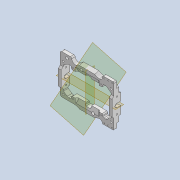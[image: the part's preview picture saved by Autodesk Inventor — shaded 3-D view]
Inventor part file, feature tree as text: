
AUTODESK INVENTOR PART (.ipt)
format: ipt  version: 2020 (Build 240168000, 168)  size: 982,528 bytes
history: native  units: mm
features: sketch x22, extrude x20, projected_geometry x20, reference x17, fillet x14, other x12, mirror x8, thicken_offset x8, plane x3, chamfer x3, hole x2
ambient origin geometry x8: Origin, YZ Plane, XZ Plane, XY Plane, X Axis, Y Axis, Z Axis, Center Point
bodies: Solid1 (feature_tree)
feature tree (129):
  extrude  "Extrusion1"  Depth=30.0mm
  extrude  "Extrusion2"  Depth=56.0mm
  plane  "Work Plane1"
  mirror  "Mirror1"
  extrude  "Extrusion3"  Depth=20.0mm
  extrude  "Extrusion4"  Depth=4.0mm TaperAngle=0.0deg
  plane  "Work Plane2"
  extrude  "Extrusion5"  Depth=10.0mm
  extrude  "Extrusion6"  Depth=1.5mm
  plane  "Work Plane3"
  mirror  "Mirror2"
  extrude  "Extrusion7"  Depth=80.0mm TaperAngle=0.0deg
  mirror  "Mirror3"
  fillet  "Fillet1"  Radius=3.0mm
  thicken_offset  "Thicken1"
  thicken_offset  "Thicken2"
  extrude  "Extrusion8"  Depth=6.0mm TaperAngle=0.0deg
  mirror  "Mirror4"
  extrude  "Extrusion10"  Depth=10.0mm
  thicken_offset  "Thicken3"
  mirror  "Mirror5"
  thicken_offset  "Thicken4"
  extrude  "Extrusion11"  Depth=3.5mm
  extrude  "Extrusion12"  Depth=10.0mm TaperAngle=0.0deg
  fillet  "Fillet4"  Radius=8.0mm
  extrude  "Extrusion13"  Depth=1.0mm
  extrude  "Extrusion14"  Depth=1.0mm
  extrude  "Extrusion15"  Depth=4.0mm
  extrude  "Extrusion16"  Depth=1.0mm
  thicken_offset  "Thicken5"
  fillet  "Fillet7"  Radius=1.5mm
  fillet  "Fillet8"  Radius=4.0mm
  fillet  "Fillet9"  Radius=3.0mm
  fillet  "Fillet10"  Radius=10.0mm
  fillet  "Fillet11"  Radius=4.0mm
  fillet  "Fillet12"  Radius=1.0mm
  extrude  "Extrusion17"  Depth=0.5mm
  mirror  "Mirror6"
  extrude  "Extrusion18"  Depth=10.0mm
  hole  "Hole1"  [1 undecoded]
  extrude  "Extrusion19"  Depth=2.8mm
  thicken_offset  "Thicken6"
  hole  "Hole2"  [1 undecoded]
  extrude  "Extrusion20"  Depth=6.0mm TaperAngle=0.0deg
  extrude  "Extrusion21"  Depth=1.0mm
  mirror  "Mirror7"
  fillet  "Fillet13"  Radius=6.0mm
  mirror  "Mirror8"
  fillet  "Fillet14"  Radius=15.0mm
  fillet  "Fillet15"  Radius=2.8mm
  chamfer  "Chamfer1"  Distance=6.0mm
  fillet  "Fillet16"  Radius=1.5mm
  chamfer  "Chamfer2"  Distance=1.5mm
  chamfer  "Chamfer3"  Distance=4.0mm
  fillet  "Fillet17"  Radius=3.0mm
  fillet  "Fillet18"  Radius=4.0mm
  thicken_offset  "Thicken7"
  thicken_offset  "Thicken8"
  sketch  "Sketch1"  dims[d0=50.0mm d1=30.0mm]
  reference  "Reference1"
  reference  "Reference2"
  sketch  "Sketch2"  dims[d2=36.0mm d3=56.0mm]
  projected_geometry  "Projected Loop1"
  reference  "Reference3"
  sketch  "Sketch3"  dims[d4=4.0mm d5=0.0mm d6=20.0mm]
  reference  "Reference4"
  sketch  "Sketch4"  dims[d7=8.0mm d8=4.0mm d9=0.0mm]
  reference  "Reference5"
  reference  "Reference6"
  sketch  "Sketch5"  dims[d10=10.0mm d11=4.0mm]
  projected_geometry  "Projected Loop2"
  projected_geometry  "Projected Loop3"
  projected_geometry  "Projected Loop4"
  reference  "Reference7"
  sketch  "Sketch6"  dims[d12=80.0mm d13=0.0mm d14=1.5mm]
  projected_geometry  "Projected Loop5"
  projected_geometry  "Projected Loop6"
  sketch  "Sketch7"  dims[d15=1.5mm d16=80.0mm d17=0.0mm d18=3.0mm]
  projected_geometry  "Projected Loop7"
  projected_geometry  "Projected Loop8"
  sketch  "Sketch8"  dims[d19=3.0mm d20=6.0mm d21=0.0mm]
  projected_geometry  "Projected Loop9"
  reference  "Reference8"
  reference  "Reference9"
  sketch  "Sketch10"  dims[d22=10.0mm d23=0.0mm d24=3.5mm]
  projected_geometry  "Projected Loop11"
  sketch  "Sketch11"  dims[d25=5.0mm d26=3.5mm]
  projected_geometry  "Projected Loop13"
  projected_geometry  "Projected Loop14"
  sketch  "Sketch12"  dims[d27=5.0mm d28=10.0mm d29=0.0mm d30=8.0mm]
  reference  "Reference11"
  sketch  "Sketch13"  dims[d32=1.0mm d33=1.0mm]
  projected_geometry  "Projected Loop15"
  sketch  "Sketch14"  dims[d34=1.0mm d35=1.0mm]
  projected_geometry  "Projected Loop16"
  sketch  "Sketch15"  dims[d36=1.5mm d37=4.0mm]
  projected_geometry  "Projected Loop17"
  sketch  "Sketch16"  dims[d38=3.0mm d39=2.0mm d40=1.5mm d41=4.0mm d42=3.0mm d43=10.0mm d44=0.0mm d49=4.0mm d50=0.0mm d51=0.5mm d52=1.0mm]
  reference  "Reference12"
  sketch  "Sketch17"  dims[d53=0.5mm d54=0.5mm]
  projected_geometry  "Projected Loop18"
  sketch  "Sketch18"  dims[d55=10.0mm d56=0.0mm d58=29.0mm]
  reference  "Reference13"
  reference  "Reference14"
  projected_geometry  "Projected Loop19"
  sketch  "Sketch19"  dims[d59=6.0mm d60=0.0mm d61=1.0mm]
  reference  "Reference15"
  sketch  "Sketch20"  dims[d63=2.0mm d64=2.8mm]
  reference  "Reference16"
  projected_geometry  "Projected Loop20"
  sketch  "Sketch21"  dims[d65=6.0mm d66=0.0mm d67=2.0mm]
  reference  "Reference17"
  sketch  "Sketch22"  dims[d68=2.8mm d69=6.0mm d70=0.0mm]
  projected_geometry  "Projected Loop21"
  reference  "Reference18"
  sketch  "Sketch23"  dims[d71=12.0mm d72=5.0mm d73=6.0mm d74=0.0mm d76=15.0mm d78=2.8mm d79=6.0mm d80=0.0mm d81=1.5mm d82=1.5mm d83=4.0mm d84=3.0mm d85=4.0mm d86=1.0mm d87=1.5mm d88=2.0mm d89=1.0mm d90=2.0mm d91=1.1mm d92=2.0mm d93=1.1mm d94=8.0mm d95=0.0mm d96=2.8mm d97=5.0mm d98=2.8mm d99=6.0mm d100=12.0mm d101=0.0mm d102=1.1mm d103=6.0mm d104=4.0mm d105=2.0mm d106=90.0deg d107=100.0mm d108=0.0mm d109=3.0mm d110=4.0mm d111=0.0mm d112=0.005mm d113=0.005mm d114=1.1mm d115=6.0mm d116=4.0mm d117=2.0mm d118=90.0deg d119=100.0mm d120=0.0mm d121=12.0mm d122=4.5mm d123=4.0mm d124=0.0mm d125=3.0mm d126=3.0mm d127=3.0mm d128=2.0mm d129=6.0mm d130=0.0mm d131=3.0mm d132=3.0mm d133=1.0mm d134=2.5mm d135=2.0mm d136=45.0deg d137=2.0mm d138=1.0mm d139=2.0mm d140=45.0deg d141=1.0mm d142=2.0mm d143=45.0deg d144=1.0mm d145=1.0mm d146=1.0mm d147=1.0mm d148=1.0mm d149=1.0mm]
  projected_geometry  "Projected Loop22"
  parser-record x1  (decoder bookkeeping rows leaked as tree rows — omitted from the tree; the rows remain in map.json)
  other  "tip_3_ass.iam"
  other  "bearing_hh_1:1"
  other  "bearing_hh_1:2"
  other  "pin_3_30:2"
  other  "roller_1:2"
  other  "roller_1:1"
  other  "c_roller_1:2"
  other  "c_roller_1:1"
  other  "bw_ass_1:1"
  other  "bw_hl_1:1"
  other  "bw_ass_1:2"
note: 2 required parameter values undecoded (feature->parameter linkage not recoverable at this tier; creation-order binding heuristic only, values carry confidence <= 0.55)
note: 1 file-system path scrubbed to <path> (originals preserved in map.json)
